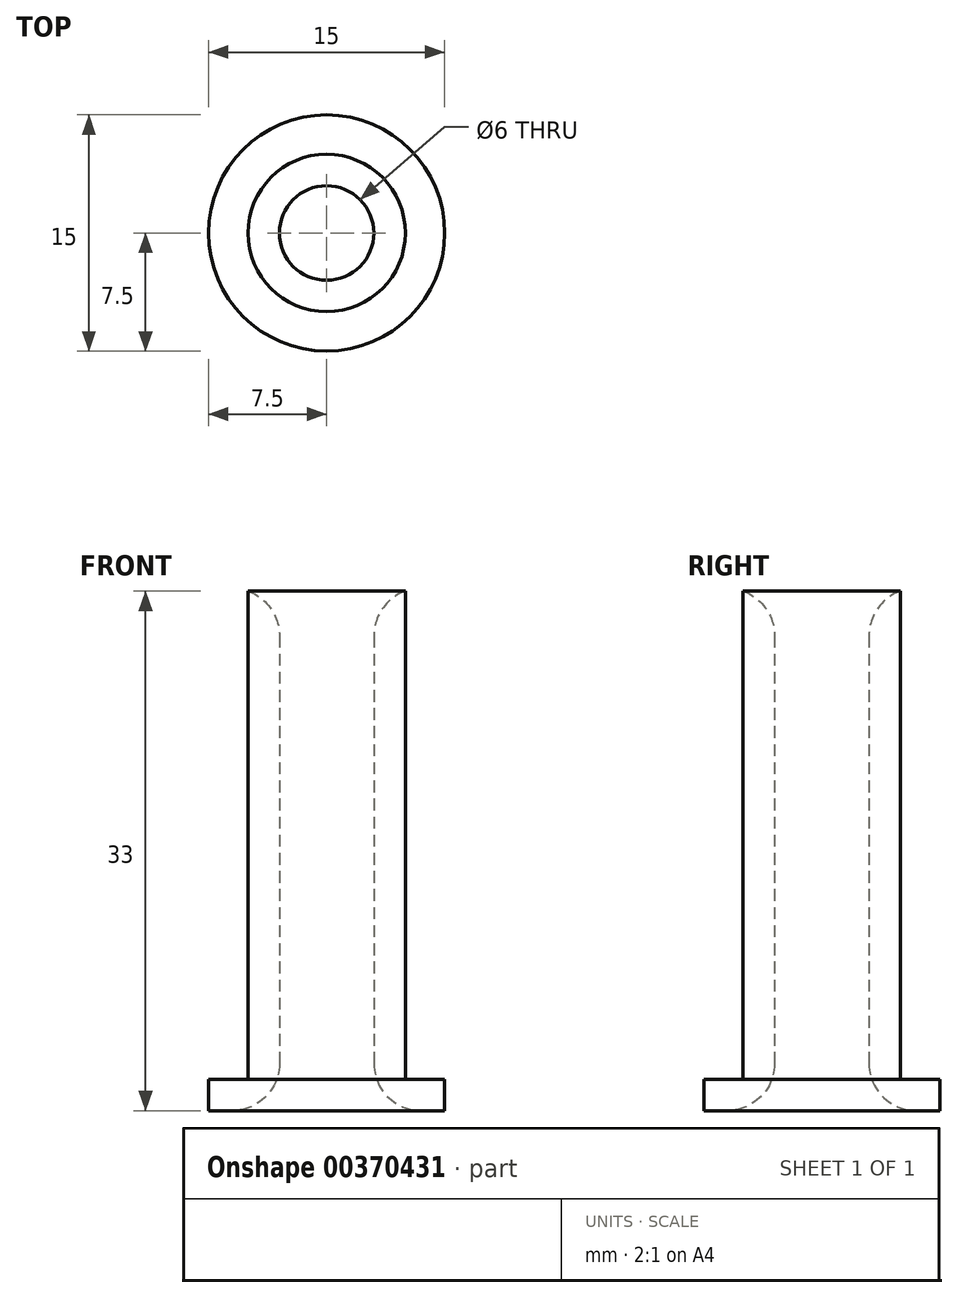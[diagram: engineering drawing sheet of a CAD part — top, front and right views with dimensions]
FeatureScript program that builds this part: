
annotation { "Feature Type Name" : "Feature", "Feature Type Description" : "" }
export const myFeature = defineFeature(function(context is Context, id is Id, definition is map)
    precondition{}
    {
        {
            var Q0;
            Q0=qCreatedBy(makeId("Top.planeOp"),FACE);
            var sketch = newSketch(context, id + "F0", { "sketchPlane" : qUnion([Q0])});
            skCircle(sketch, "E0", {"center": v(0, 0) * mm, "radius": 7.5 * mm});
            skCircle(sketch, "E1", {"center": v(0, 0) * mm, "radius": 3 * mm});
            skCircle(sketch, "E2", {"center": v(0, 0) * mm, "radius": 5 * mm});
            skSolve(sketch);
        }
        {
            var Q0;
            Q0=makeQuery(id+"F0.imprint","IMPRINT",FACE,{"disambiguationData":[TD([[makeQuery(id+"F0.imprint","IMPRINT",EDGE,{"derivedFrom":sQuery(id+"F0.wireOp",EDGE,"E0")}),1.0]])]});
            extrude(context, id + "F1", {"entities" : qUnion([Q0]), "depth" : 2 * mm});
        }
        {
            var Q0;
            Q0=makeQuery(id+"F0.imprint","IMPRINT",FACE,{"disambiguationData":[TD([[makeQuery(id+"F0.imprint","IMPRINT",EDGE,{"derivedFrom":sQuery(id+"F0.wireOp",EDGE,"E1")}),-1.0]])]});
            extrude(context, id + "F2", {"entities" : qUnion([Q0]), "operationType" : NewBodyOperationType.ADD, "depth" : 33 * mm});
        }
        {
            var Q0;
            Q0=makeQuery(id+"F2.opExtrude","CAP_EDGE",EDGE,{"disambiguationData":[OSD([sQuery(id+"F0.wireOp",EDGE,"E1")])],"isStart":true});
            var Q1;
            Q1=makeQuery(id+"F2.opExtrude","CAP_EDGE",EDGE,{"disambiguationData":[OSD([sQuery(id+"F0.wireOp",EDGE,"E1")])],"isStart":false});
            fillet(context, id + "F3", {"entities" : qUnion([Q0, Q1]), "radius" : 3 * mm, "tangentPropagation" : true, "allowEdgeOverflow" : false});
        }
    });
